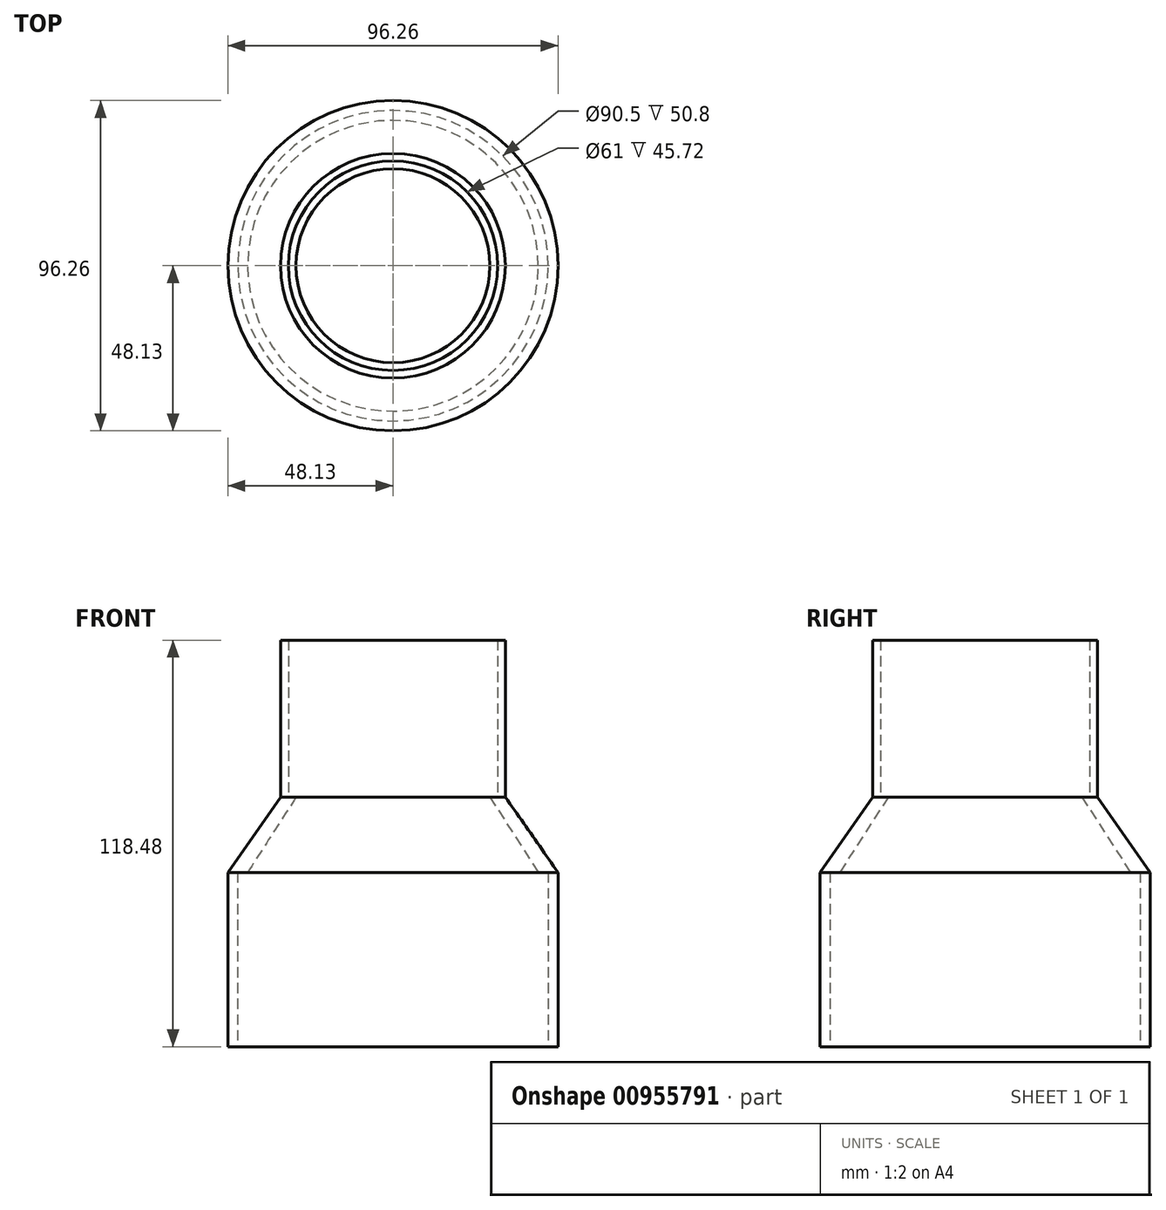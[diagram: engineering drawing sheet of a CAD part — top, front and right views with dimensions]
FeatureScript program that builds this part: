
annotation { "Feature Type Name" : "Feature", "Feature Type Description" : "" }
export const myFeature = defineFeature(function(context is Context, id is Id, definition is map)
    precondition{}
    {
        {
            var Q0;
            Q0=qCreatedBy(makeId("Top.planeOp"),FACE);
            var sketch = newSketch(context, id + "F0", { "sketchPlane" : qUnion([Q0])});
            skCircle(sketch, "E0", {"center": v(0, 0) * mm, "radius": 45.25 * mm});
            skCircle(sketch, "E1", {"center": v(0, 0) * mm, "radius": 48.12 * mm});
            skSolve(sketch);
        }
        {
            var Q0;
            Q0=makeQuery(id+"F0.imprint","IMPRINT",FACE,{"disambiguationData":[TD([[makeQuery(id+"F0.imprint","IMPRINT",EDGE,{"derivedFrom":sQuery(id+"F0.wireOp",EDGE,"E0")}),-1.0]])]});
            extrude(context, id + "F1", {"entities" : qUnion([Q0]), "depth" : 50.8 * mm, "offsetDistance" : 25 * mm});
        }
        {
            var Q0;
            Q0=makeQuery(id+"F1.opExtrude","CAP_FACE",FACE,{"disambiguationData":[OSD([sQuery(id+"F0.wireOp",EDGE,"E0"),sQuery(id+"F0.wireOp",EDGE,"E1")])],"isStart":false});
            cPlane(context, id + "F2", {"entities" : qUnion([Q0]), "cplaneType" : CPlaneType.OFFSET, "offset" : 21.96 * mm, "width" : 150 * mm, "height" : 150 * mm});
        }
        {
            var Q0;
            Q0=qCreatedBy(id+"F2.planeOp",FACE);
            var sketch = newSketch(context, id + "F3", { "sketchPlane" : qUnion([Q0])});
            skCircle(sketch, "E2", {"center": v(0, 0) * mm, "radius": 32.75 * mm});
            skSolve(sketch);
        }
        {
            var Q0;
            Q0=makeQuery(id+"F1.opExtrude","CAP_FACE",FACE,{"disambiguationData":[OSD([sQuery(id+"F0.wireOp",EDGE,"E0"),sQuery(id+"F0.wireOp",EDGE,"E1")])],"isStart":false});
            var sketch = newSketch(context, id + "F4", { "sketchPlane" : qUnion([Q0])});
            skCircle(sketch, "E3.0.0", {"center": v(0, 0) * mm, "radius": 48.12 * mm});
            skSolve(sketch);
        }
        {
            var Q1;
            Q1 = qSketchRegion(id + "F4", true);
            var Q2;
            Q2=makeQuery(id+"F3.imprint","IMPRINT",FACE,{"disambiguationData":[TD([[makeQuery(id+"F3.imprint","IMPRINT",EDGE,{"derivedFrom":sQuery(id+"F3.wireOp",EDGE,"E2")}),1.0]])]});
            loft(context, id + "F5", {"operationType" : NewBodyOperationType.ADD, "sheetProfilesArray" : [{ "sheetProfileEntities" : qUnion([Q1]) }, { "sheetProfileEntities" : qUnion([Q2]) }]});
        }
        {
            var Q0;
            {var subQ0=makeQuery(id+"F4.imprint","IMPRINT",EDGE,{"derivedFrom":makeQuery(id+"F1.opExtrude","CAP_EDGE",EDGE,{"disambiguationData":[OSD([sQuery(id+"F0.wireOp",EDGE,"E0")])],"isStart":false})});Q0=makeQuery(id+"F5.opLoft","CAP_FACE",FACE,{"disambiguationData":[OSD([makeQuery(id+"F4.imprint","IMPRINT",FACE,{"disambiguationData":[TD([[makeQuery(id+"F4.imprint","IMPRINT",EDGE,{"derivedFrom":sQuery(id+"F4.wireOp",EDGE,"E3.0.0")}),1.0]])]}),makeQuery(id+"F4.imprint","IMPRINT",FACE,{"disambiguationData":[TD([[subQ0,1.0]])]})])],"isStart":true});}
            var sketch = newSketch(context, id + "F6", { "sketchPlane" : qUnion([Q0])});
            skCircle(sketch, "E4.0", {"center": v(0, 0) * mm, "radius": 45.25 * mm});
            skCircle(sketch, "E5", {"center": v(0, 0) * mm, "radius": 42.38 * mm});
            skSolve(sketch);
        }
        {
            var Q0;
            Q0=makeQuery(id+"F5.opLoft","CAP_FACE",FACE,{"disambiguationData":[OSD([makeQuery(id+"F3.imprint","IMPRINT",FACE,{"disambiguationData":[TD([[makeQuery(id+"F3.imprint","IMPRINT",EDGE,{"derivedFrom":sQuery(id+"F3.wireOp",EDGE,"E2")}),1.0]])]})])],"isStart":true});
            var sketch = newSketch(context, id + "F7", { "sketchPlane" : qUnion([Q0])});
            skCircle(sketch, "E6.0.0", {"center": v(0, 0) * mm, "radius": 32.75 * mm});
            skCircle(sketch, "E7", {"center": v(0, 0) * mm, "radius": 28.25 * mm});
            skSolve(sketch);
        }
        {
            var Q1;
            Q1=makeQuery(id+"F7.imprint","IMPRINT",FACE,{"disambiguationData":[TD([[makeQuery(id+"F7.imprint","IMPRINT",EDGE,{"derivedFrom":sQuery(id+"F7.wireOp",EDGE,"E7")}),1.0]])]});
            var Q2;
            Q2=makeQuery(id+"F6.imprint","IMPRINT",FACE,{"disambiguationData":[TD([[makeQuery(id+"F6.imprint","IMPRINT",EDGE,{"derivedFrom":sQuery(id+"F6.wireOp",EDGE,"E5")}),1.0]])]});
            loft(context, id + "F8", {"operationType" : NewBodyOperationType.REMOVE, "sheetProfilesArray" : [{ "sheetProfileEntities" : qUnion([Q1]) }, { "sheetProfileEntities" : qUnion([Q2]) }]});
        }
        {
            var Q0;
            Q0=makeQuery(id+"F5.opLoft","CAP_FACE",FACE,{"disambiguationData":[OSD([makeQuery(id+"F3.imprint","IMPRINT",FACE,{"disambiguationData":[TD([[makeQuery(id+"F3.imprint","IMPRINT",EDGE,{"derivedFrom":sQuery(id+"F3.wireOp",EDGE,"E2")}),1.0]])]})])],"isStart":true});
            var sketch = newSketch(context, id + "F9", { "sketchPlane" : qUnion([Q0])});
            skCircle(sketch, "E8", {"center": v(0, 0) * mm, "radius": 30.5 * mm});
            skSolve(sketch);
        }
        {
            var Q0;
            Q0=makeQuery(id+"F9.imprint","IMPRINT",FACE,{"disambiguationData":[TD([[makeQuery(id+"F9.imprint","IMPRINT",EDGE,{"derivedFrom":sQuery(id+"F9.wireOp",EDGE,"E8")}),-1.0]])]});
            extrude(context, id + "F10", {"entities" : qUnion([Q0]), "operationType" : NewBodyOperationType.ADD, "depth" : 45.72 * mm, "offsetDistance" : 25 * mm});
        }
    });
